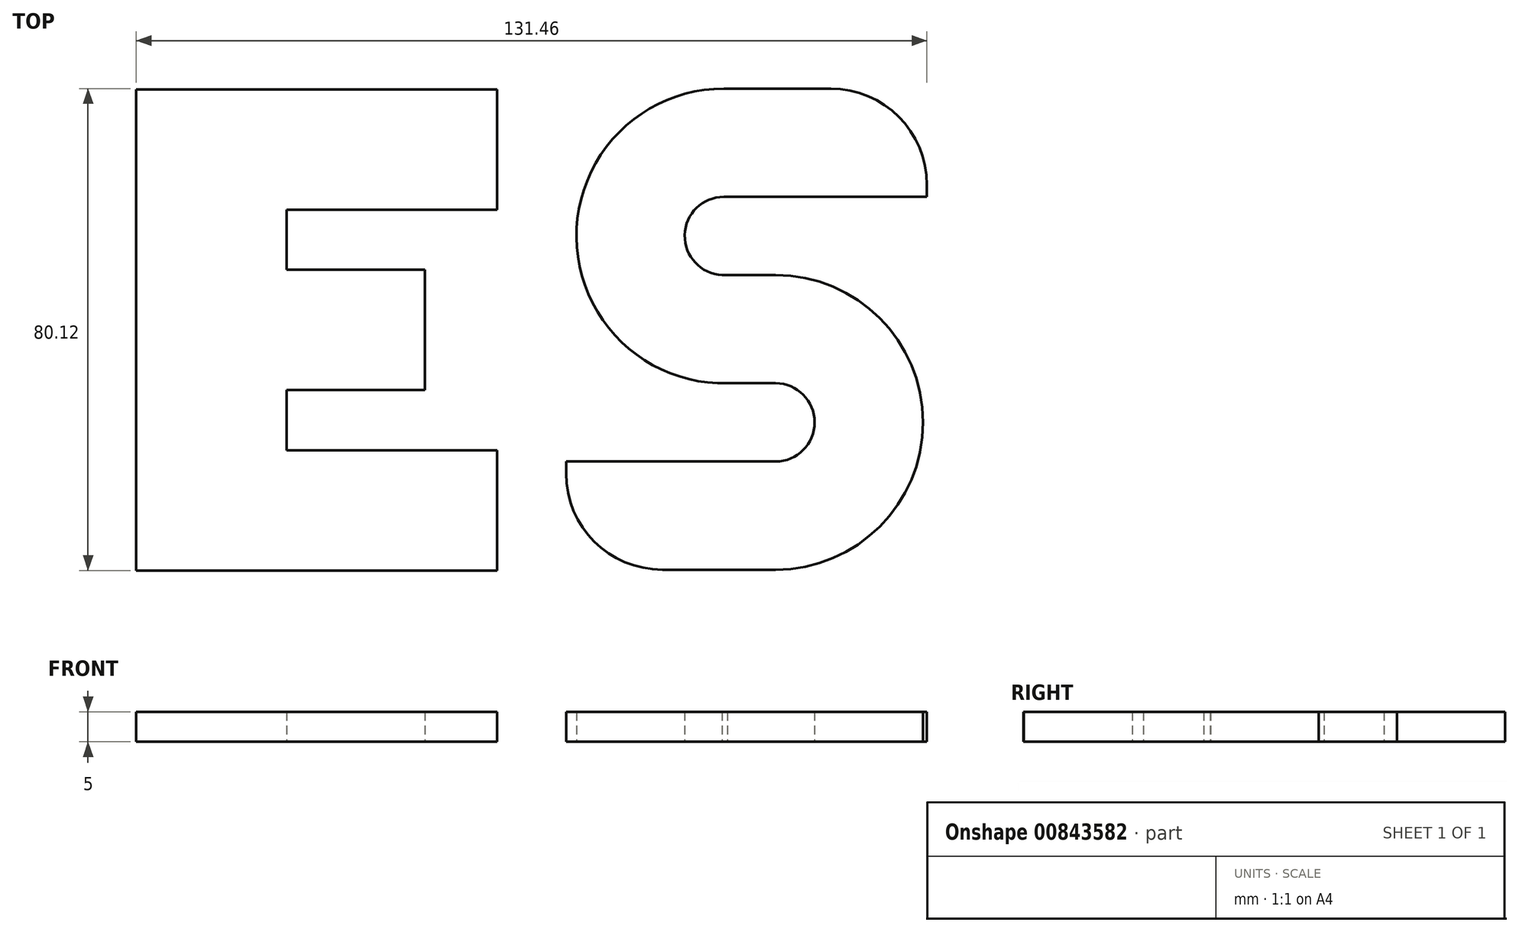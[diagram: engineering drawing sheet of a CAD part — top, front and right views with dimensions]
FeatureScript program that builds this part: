
annotation { "Feature Type Name" : "Feature", "Feature Type Description" : "" }
export const myFeature = defineFeature(function(context is Context, id is Id, definition is map)
    precondition{}
    {
        {
            var Q0;
            Q0=qCreatedBy(makeId("Top.planeOp"),FACE);
            var sketch = newSketch(context, id + "F0", { "sketchPlane" : qUnion([Q0])});
            skPoint(sketch, "E0.middle", {"position": v(0, 0) * mm});
            skLineSegment(sketch, "E1.bottom", {"start": v(-69.42, -11.8) * mm, "end": v(-9.42, -11.8) * mm});
            skLineSegment(sketch, "E1.top", {"start": v(-69.42, -91.8) * mm, "end": v(-9.42, -91.8) * mm});
            skLineSegment(sketch, "E1.left", {"start": v(-69.42, -11.8) * mm, "end": v(-69.42, -91.8) * mm});
            skLineSegment(sketch, "E1.right", {"start": v(-9.42, -11.8) * mm, "end": v(-9.42, -31.8) * mm});
            skLineSegment(sketch, "E2", {"start": v(-44.42, -31.8) * mm, "end": v(-9.42, -31.8) * mm});
            skLineSegment(sketch, "E3", {"start": v(-44.42, -71.8) * mm, "end": v(-9.42, -71.8) * mm});
            skLineSegment(sketch, "E4", {"start": v(-44.42, -41.8) * mm, "end": v(-21.42, -41.8) * mm});
            skLineSegment(sketch, "E5", {"start": v(-44.42, -61.8) * mm, "end": v(-21.42, -61.8) * mm});
            skLineSegment(sketch, "E6", {"start": v(-44.42, -31.8) * mm, "end": v(-44.42, -41.8) * mm});
            skPoint(sketch, "E7.orphan", {"position": v(0, -61.8) * mm});
            skLineSegment(sketch, "E8.trimOffspring", {"start": v(-9.42, -71.8) * mm, "end": v(-9.42, -91.8) * mm});
            skLineSegment(sketch, "E9.trimOffspring", {"start": v(-44.42, -61.8) * mm, "end": v(-44.42, -71.8) * mm});
            skLineSegment(sketch, "E10", {"start": v(-21.42, -41.8) * mm, "end": v(-21.42, -61.8) * mm});
            skLineSegment(sketch, "E11.bottom", {"start": v(28.27, -11.69) * mm, "end": v(46.04, -11.69) * mm});
            skLineSegment(sketch, "E11.top", {"start": v(18.04, -91.69) * mm, "end": v(36.87, -91.69) * mm});
            skLineSegment(sketch, "E11.right", {"start": v(62.04, -27.69) * mm, "end": v(62.04, -29.69) * mm});
            skLineSegment(sketch, "E12", {"start": v(28.27, -29.69) * mm, "end": v(62.04, -29.69) * mm});
            skLineSegment(sketch, "E13", {"start": v(2.04, -73.69) * mm, "end": v(36.87, -73.69) * mm});
            skLineSegment(sketch, "E14", {"start": v(27.96, -42.69) * mm, "end": v(36.87, -42.69) * mm});
            skLineSegment(sketch, "E15.trimOffspring", {"start": v(2.04, -73.69) * mm, "end": v(2.04, -75.69) * mm});
            skArc(sketch, "E16", {"start": v(36.87, -73.69) * mm, "mid": v(43.37, -67.19) * mm, "end": v(36.87, -60.69) * mm});
            skPoint(sketch, "E16.centerSnap0", {"position": v(43.37, -67.19) * mm});
            skPoint(sketch, "E17.orphan", {"position": v(43.37, -60.69) * mm});
            skPoint(sketch, "E18.end.orphan", {"position": v(43.37, -73.69) * mm});
            skLineSegment(sketch, "E19", {"start": v(28.86, -60.69) * mm, "end": v(36.87, -60.69) * mm});
            skArc(sketch, "E20", {"start": v(36.87, -91.69) * mm, "mid": v(61.37, -67.19) * mm, "end": v(36.87, -42.69) * mm});
            skArc(sketch, "E21", {"start": v(28.27, -29.69) * mm, "mid": v(21.77, -36.34) * mm, "end": v(28.57, -42.69) * mm});
            skArc(sketch, "E22", {"start": v(28.27, -11.69) * mm, "mid": v(3.77, -36.49) * mm, "end": v(28.86, -60.69) * mm});
            skPoint(sketch, "E23.visualSharp", {"position": v(62.04, -11.69) * mm});
            skArc(sketch, "E23.filletArc", {"start": v(62.04, -27.69) * mm, "mid": v(57.35, -16.37) * mm, "end": v(46.04, -11.69) * mm});
            skPoint(sketch, "E24.visualSharp", {"position": v(2.04, -91.69) * mm});
            skArc(sketch, "E24.filletArc", {"start": v(2.04, -75.69) * mm, "mid": v(6.73, -87) * mm, "end": v(18.04, -91.69) * mm});
            skSolve(sketch);
        }
        {
            var Q0;
            Q0 = qSketchRegion(id + "F0", true);
            extrude(context, id + "F1", {"entities" : qUnion([Q0]), "depth" : 5 * mm, "offsetDistance" : 25 * mm});
        }
    });
